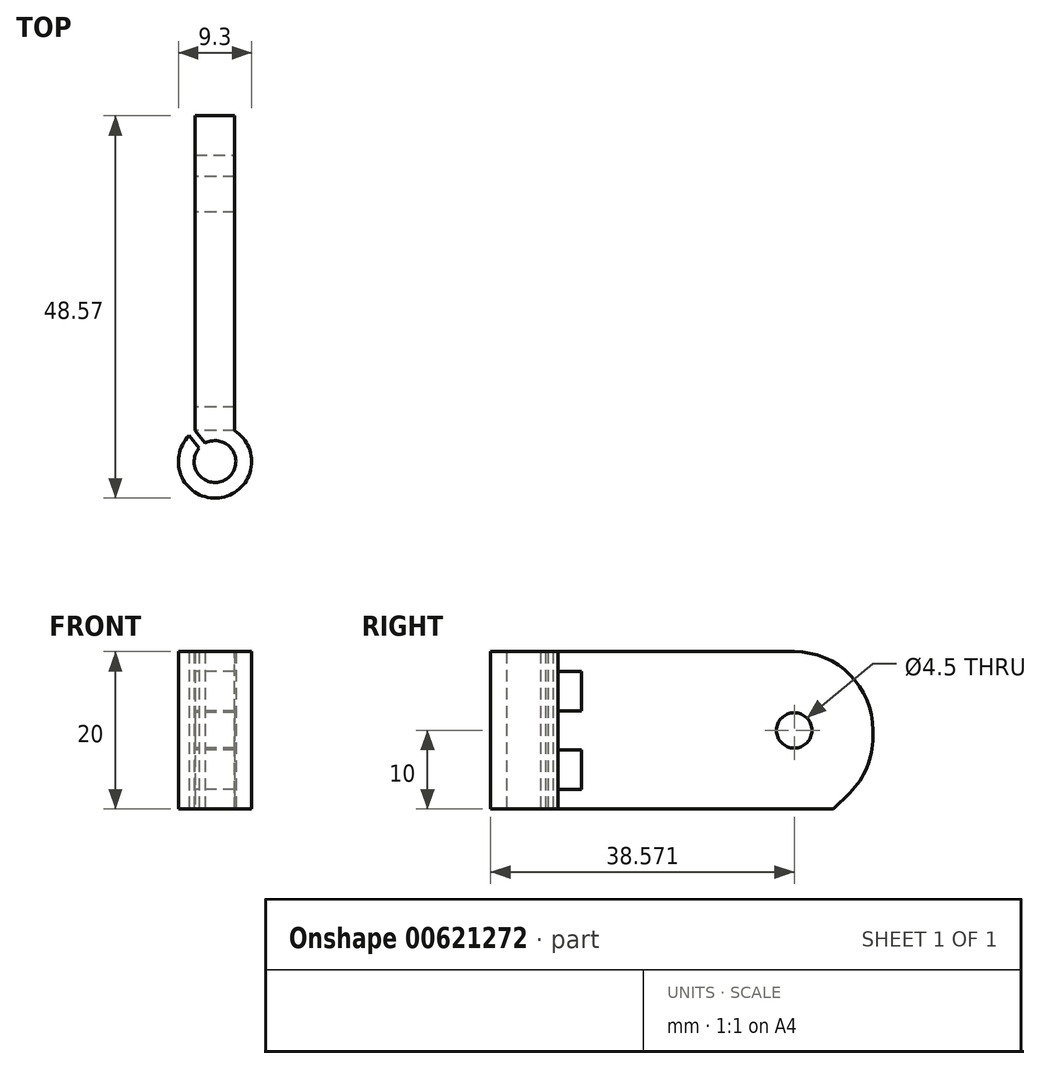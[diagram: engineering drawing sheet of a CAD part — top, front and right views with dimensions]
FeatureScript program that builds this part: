
annotation { "Feature Type Name" : "Feature", "Feature Type Description" : "" }
export const myFeature = defineFeature(function(context is Context, id is Id, definition is map)
    precondition{}
    {
        {
            var Q0;
            Q0=qCreatedBy(makeId("Top.planeOp"),FACE);
            var sketch = newSketch(context, id + "F0", { "sketchPlane" : qUnion([Q0])});
            skCircle(sketch, "E0", {"center": v(0, 0) * mm, "radius": 2.65 * mm});
            skCircle(sketch, "E1", {"center": v(0, 0) * mm, "radius": 4.65 * mm});
            skLineSegment(sketch, "E2", {"start": v(-2.5, 3.92) * mm, "end": v(-2.5, 43.92) * mm});
            skLineSegment(sketch, "E3", {"start": v(-2.5, 43.92) * mm, "end": v(2.5, 43.92) * mm});
            skLineSegment(sketch, "E4", {"start": v(2.5, 43.92) * mm, "end": v(2.5, 3.92) * mm});
            skLineSegment(sketch, "E5", {"start": v(0, 0) * mm, "end": v(0, 43.92) * mm});
            skLineSegment(sketch, "E6", {"start": v(-2.5, 3.92) * mm, "end": v(-1.24, 2.34) * mm});
            skLineSegment(sketch, "E7", {"start": v(-3.28, 3.3) * mm, "end": v(-2.02, 1.72) * mm});
            skLineSegment(sketch, "E8", {"start": v(-2.65, 2.5) * mm, "end": v(-1.87, 3.13) * mm});
            skLineSegment(sketch, "E9", {"start": v(-2.26, 2.82) * mm, "end": v(0, 0) * mm});
            skSolve(sketch);
        }
        {
            var Q0;
            {var subQ2=sQuery(id+"F0.wireOp",EDGE,"E7");var subQ4=sQuery(id+"F0.wireOp",EDGE,"E0");var subQ5=makeQuery(id+"F0.imprint","INTERSECT",VERTEX,{"derivedFrom":[subQ4,subQ2]});Q0=makeQuery(id+"F0.imprint","IMPRINT",FACE,{"disambiguationData":[TD([[makeQuery(id+"F0.imprint","IMPRINT",EDGE,{"disambiguationData":[TD([[subQ5,-1.0]])],"derivedFrom":subQ4}),-1.0]])]});}
            var Q1;
            {var subQ0=sQuery(id+"F0.wireOp",EDGE,"E4");Q1=makeQuery(id+"F0.imprint","IMPRINT",FACE,{"disambiguationData":[TD([[makeQuery(id+"F0.imprint","IMPRINT",EDGE,{"derivedFrom":subQ0}),-1.0]])]});}
            var Q2;
            {var subQ1=sQuery(id+"F0.wireOp",EDGE,"E0");var subQ5=sQuery(id+"F0.wireOp",EDGE,"E6");var subQ8=makeQuery(id+"F0.imprint","INTERSECT",VERTEX,{"derivedFrom":[subQ1,subQ5]});Q2=makeQuery(id+"F0.imprint","IMPRINT",FACE,{"disambiguationData":[TD([[makeQuery(id+"F0.imprint","IMPRINT",EDGE,{"disambiguationData":[TD([[subQ8,1.0]])],"derivedFrom":subQ1}),-1.0]])]});}
            var Q3;
            {var subQ0=sQuery(id+"F0.wireOp",EDGE,"E2");Q3=makeQuery(id+"F0.imprint","IMPRINT",FACE,{"disambiguationData":[TD([[makeQuery(id+"F0.imprint","IMPRINT",EDGE,{"derivedFrom":subQ0}),-1.0]])]});}
            extrude(context, id + "F1", {"entities" : qUnion([Q0, Q1, Q2, Q3]), "depth" : 20 * mm, "offsetDistance" : 25 * mm});
        }
        {
            var Q0;
            Q0=makeQuery(id+"F1.opExtrude","SWEPT_FACE",FACE,{"disambiguationData":[OSD([sQuery(id+"F0.wireOp",EDGE,"E2")])]});
            var sketch = newSketch(context, id + "F2", { "sketchPlane" : qUnion([Q0])});
            skCircle(sketch, "E10", {"center": v(-33.92, 10) * mm, "radius": 2.25 * mm});
            skLineSegment(sketch, "E11", {"start": v(-33.92, 10) * mm, "end": v(-33.92, 20) * mm});
            skLineSegment(sketch, "E12", {"start": v(-33.92, 10) * mm, "end": v(-43.92, 10) * mm});
            skPoint(sketch, "E12.endSnap0", {"position": v(-43.92, 10) * mm});
            skLineSegment(sketch, "E13.bottom", {"start": v(-6.92, 17.5) * mm, "end": v(-3.92, 17.5) * mm});
            skLineSegment(sketch, "E13.top", {"start": v(-6.92, 12.5) * mm, "end": v(-3.92, 12.5) * mm});
            skLineSegment(sketch, "E13.left", {"start": v(-6.92, 17.5) * mm, "end": v(-6.92, 12.5) * mm});
            skLineSegment(sketch, "E13.right", {"start": v(-3.92, 17.5) * mm, "end": v(-3.92, 12.5) * mm});
            skLineSegment(sketch, "E14.bottom", {"start": v(-6.92, 2.5) * mm, "end": v(-3.92, 2.5) * mm});
            skLineSegment(sketch, "E14.top", {"start": v(-6.92, 7.5) * mm, "end": v(-3.92, 7.5) * mm});
            skLineSegment(sketch, "E14.left", {"start": v(-6.92, 2.5) * mm, "end": v(-6.92, 7.5) * mm});
            skLineSegment(sketch, "E14.right", {"start": v(-3.92, 2.5) * mm, "end": v(-3.92, 7.5) * mm});
            skLineSegment(sketch, "E15", {"start": v(-5.42, 17.5) * mm, "end": v(-5.42, 20) * mm});
            skLineSegment(sketch, "E16", {"start": v(-5.42, 2.5) * mm, "end": v(-5.42, 0) * mm});
            skSolve(sketch);
        }
        {
            var Q0;
            {var subQ0=sQuery(id+"F2.wireOp",EDGE,"E11");var subQ1=sQuery(id+"F2.wireOp",EDGE,"E10");var subQ2=makeQuery(id+"F2.imprint","INTERSECT",VERTEX,{"derivedFrom":[subQ1,subQ0]});Q0=makeQuery(id+"F2.imprint","IMPRINT",FACE,{"disambiguationData":[TD([[makeQuery(id+"F2.imprint","IMPRINT",EDGE,{"disambiguationData":[TD([[subQ2,-1.0]])],"derivedFrom":subQ1}),1.0]])]});}
            var Q1;
            {var subQ0=sQuery(id+"F2.wireOp",EDGE,"E11");var subQ1=sQuery(id+"F2.wireOp",EDGE,"E10");var subQ2=makeQuery(id+"F2.imprint","INTERSECT",VERTEX,{"derivedFrom":[subQ1,subQ0]});Q1=makeQuery(id+"F2.imprint","IMPRINT",FACE,{"disambiguationData":[TD([[makeQuery(id+"F2.imprint","IMPRINT",EDGE,{"disambiguationData":[TD([[subQ2,1.0]])],"derivedFrom":subQ1}),1.0]])]});}
            var Q2;
            Q2=makeQuery(id+"F2.imprint","IMPRINT",FACE,{"disambiguationData":[TD([[makeQuery(id+"F2.imprint","IMPRINT",EDGE,{"derivedFrom":sQuery(id+"F2.wireOp",EDGE,"E13.top")}),1.0]])]});
            var Q3;
            Q3=makeQuery(id+"F2.imprint","IMPRINT",FACE,{"disambiguationData":[TD([[makeQuery(id+"F2.imprint","IMPRINT",EDGE,{"derivedFrom":sQuery(id+"F2.wireOp",EDGE,"E14.top")}),-1.0]])]});
            extrude(context, id + "F3", {"entities" : qUnion([Q0, Q1, Q2, Q3]), "operationType" : NewBodyOperationType.REMOVE, "endBound" : BoundingType.THROUGH_ALL, "oppositeDirection" : true, "depth" : 25 * mm, "offsetDistance" : 25 * mm});
        }
        {
            var Q0;
            Q0=makeQuery(id+"F1.opExtrude","CAP_EDGE",EDGE,{"disambiguationData":[OSD([sQuery(id+"F0.wireOp",EDGE,"E3")])],"isStart":false});
            fillet(context, id + "F4", {"entities" : qUnion([Q0]), "radius" : 10 * mm, "tangentPropagation" : true, "allowEdgeOverflow" : false});
        }
        {
            var Q0;
            Q0=makeQuery(id+"F1.opExtrude","CAP_EDGE",EDGE,{"disambiguationData":[OSD([sQuery(id+"F0.wireOp",EDGE,"E3")])],"isStart":true});
            chamfer(context, id + "F5", {"entities" : qUnion([Q0]), "width" : 5 * mm, "tangentPropagation" : true});
        }
        {
            var Q0;
            {var subQ0=sQuery(id+"F0.wireOp",EDGE,"E3");Q0=makeQuery(id+"F5.opChamfer","BLEND_EDGE",EDGE,{"blendedFrom":[makeQuery(id+"F1.opExtrude","CAP_EDGE",EDGE,{"disambiguationData":[OSD([subQ0])],"isStart":true}),makeQuery(id+"F1.opExtrude","SWEPT_FACE",FACE,{"disambiguationData":[OSD([subQ0])]})],"blendedInto":[makeQuery(id+"F1.opExtrude","SWEPT_FACE",FACE,{"disambiguationData":[OSD([subQ0])]})]});}
            fillet(context, id + "F6", {"entities" : qUnion([Q0]), "radius" : 10 * mm, "tangentPropagation" : true, "allowEdgeOverflow" : false});
        }
    });
